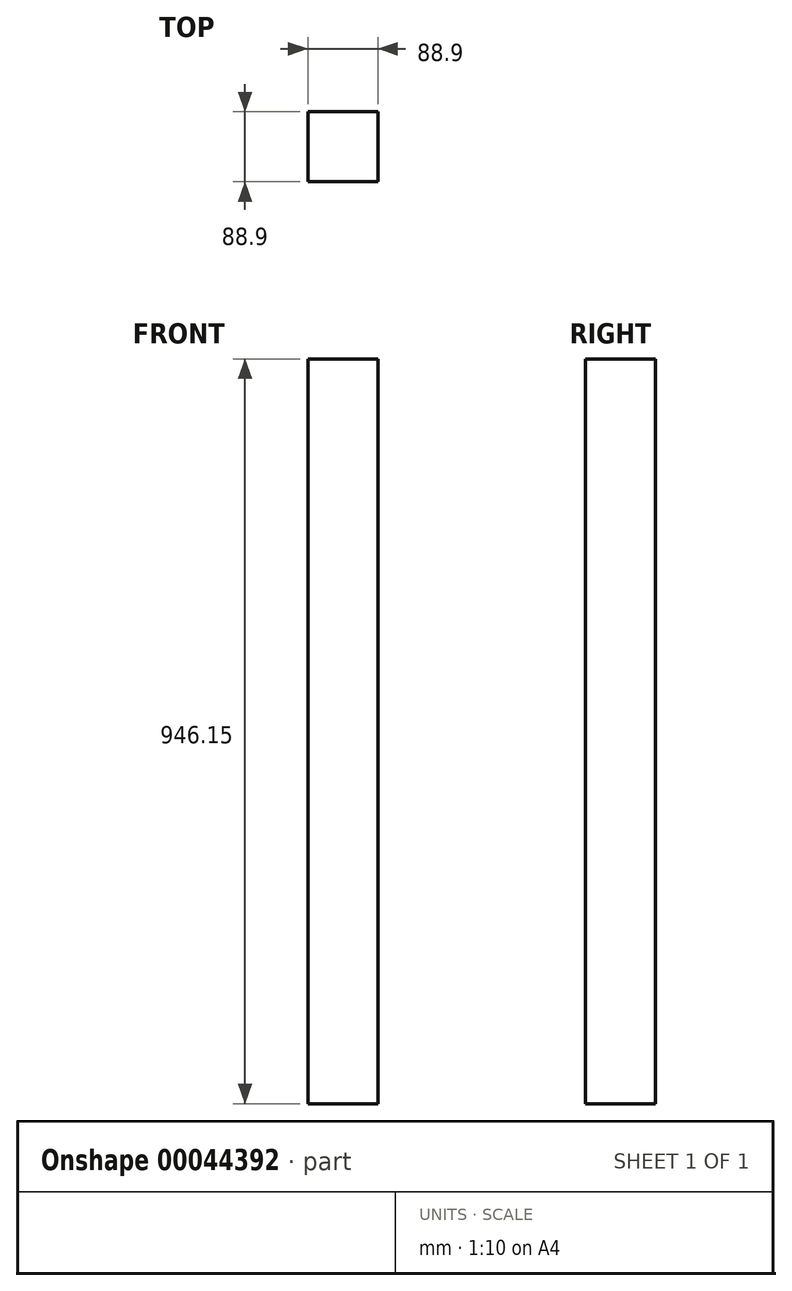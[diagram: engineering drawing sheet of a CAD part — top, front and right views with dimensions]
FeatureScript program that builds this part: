
annotation { "Feature Type Name" : "Feature", "Feature Type Description" : "" }
export const myFeature = defineFeature(function(context is Context, id is Id, definition is map)
    precondition{}
    {
        {
            var Q0;
            Q0=qCreatedBy(makeId("Top.planeOp"),FACE);
            var sketch = newSketch(context, id + "F0", { "sketchPlane" : qUnion([Q0])});
            skLineSegment(sketch, "E0.bottom", {"start": v(-44.45, 44.45) * mm, "end": v(44.45, 44.45) * mm});
            skLineSegment(sketch, "E0.top", {"start": v(-44.45, -44.45) * mm, "end": v(44.45, -44.45) * mm});
            skLineSegment(sketch, "E0.left", {"start": v(-44.45, 44.45) * mm, "end": v(-44.45, -44.45) * mm});
            skLineSegment(sketch, "E0.right", {"start": v(44.45, 44.45) * mm, "end": v(44.45, -44.45) * mm});
            skSolve(sketch);
        }
        {
            var Q0;
            Q0=makeQuery(id+"F0.imprint","IMPRINT",FACE,{"disambiguationData":[TD([[makeQuery(id+"F0.imprint","IMPRINT",EDGE,{"derivedFrom":sQuery(id+"F0.wireOp",EDGE,"E0.bottom")}),-1.0]])]});
            extrude(context, id + "F1", {"entities" : qUnion([Q0]), "depth" : 946.15 * mm});
        }
    });
